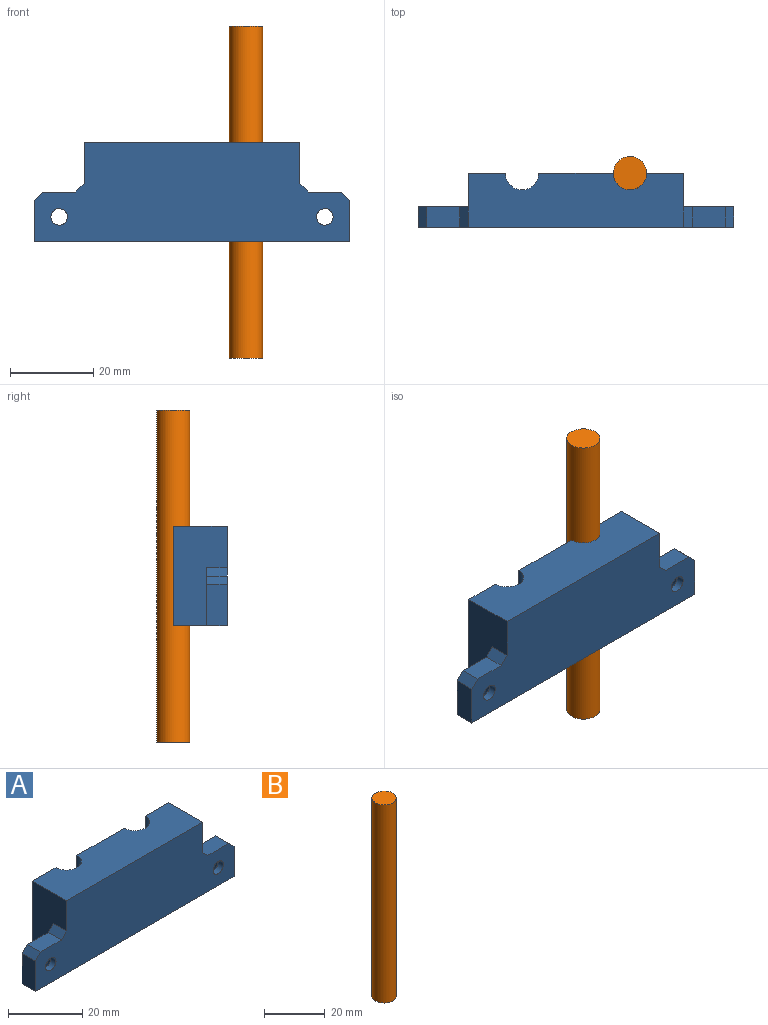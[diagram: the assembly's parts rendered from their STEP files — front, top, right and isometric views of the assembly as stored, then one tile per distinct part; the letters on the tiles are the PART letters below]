
ASSEMBLY  parts=2 mates=1
PART A: 32 faces, bbox 76x13x24 mm
  f0: plane 24x13mm, normal (-1,0,0), area 242mm2, adj f4,f5,f6,f9,f21,f27
  f1: plane 24x12mm, normal (0,0,-1), area 169.6mm2, adj f2,f4,f7,f8
  f2: plane 24x18mm, normal (0,1,0), area 192mm2, adj f1,f3,f6,f7,f8,f9,f10,f11
  f3: cylinder r=4mm len=24mm, axis (0,0,-1), area 301.6mm2, adj f2,f4,f6,f9
  f4: plane 24x9mm, normal (0,1,0), area 96mm2, adj f0,f1,f3,f6,f7,f8,f9,f10
  f5: plane 76x24mm, normal (0,-1,0), area 1510.9mm2, adj f0,f6,f9,f14,f18,f19,f20,f22
  f6: plane 52x13mm, normal (0,0,1), area 625.7mm2, adj f0,f2,f3,f4,f5,f12,f13,f14
  f7: cylinder r=12mm len=24mm, axis (0,0,-1), area 754mm2, adj f1,f2,f4,f10
  f8: cylinder r=6mm len=20mm, axis (0,0,-1), area 377mm2, adj f1,f2,f4,f10
  f9: plane 76x13mm, normal (0,0,-1), area 745.7mm2, adj f0,f2,f3,f4,f5,f12,f13,f14
  f10: plane 24x12mm, normal (0,0,1), area 169.6mm2, adj f2,f4,f7,f8
  f11: plane 24x12mm, normal (0,0,-1), area 169.6mm2, adj f2,f12,f15,f16
  f12: plane 24x9mm, normal (0,1,0), area 96mm2, adj f6,f9,f11,f13,f14,f15,f16,f17
  f13: cylinder r=4mm len=24mm, axis (0,0,-1), area 301.6mm2, adj f2,f6,f9,f12
  f14: plane 24x13mm, normal (1,0,0), area 242mm2, adj f5,f6,f9,f12,f25,f28
  f15: cylinder r=12mm len=24mm, axis (0,0,-1), area 754mm2, adj f2,f11,f12,f17
  f16: cylinder r=6mm len=20mm, axis (0,0,-1), area 377mm2, adj f2,f11,f12,f17
  f17: plane 24x12mm, normal (0,0,1), area 169.6mm2, adj f2,f12,f15,f16
  f18: plane 8x5mm, normal (0,0,1), area 40mm2, adj f5,f21,f26,f27
  f19: plane 10x5mm, normal (-1,0,0), area 50mm2, adj f5,f9,f21,f26
  f20: cylinder r=2mm len=4mm, axis (0,-1,0), area 25.1mm2, adj f5,f31
  f21: plane 14x12mm, normal (0,1,0), area 65.5mm2, adj f0,f9,f18,f19,f26,f27,f31
  f22: plane 10x5mm, normal (1,0,0), area 50mm2, adj f5,f9,f25,f29
  f23: plane 8x5mm, normal (0,0,1), area 40mm2, adj f5,f25,f28,f29
  f24: cylinder r=2mm len=4mm, axis (0,-1,0), area 25.1mm2, adj f5,f30
  f25: plane 14x12mm, normal (0,1,0), area 65.5mm2, adj f9,f14,f22,f23,f28,f29,f30
  f26: plane 5x2mm, normal (-0.71,0,0.71), area 14.1mm2, adj f5,f18,f19,f21
  f27: plane 5x2mm, normal (-0.71,0,0.71), area 14.1mm2, adj f0,f5,f18,f21
  f28: plane 5x2mm, normal (0.71,0,0.71), area 14.1mm2, adj f5,f14,f23,f25
  f29: plane 5x2mm, normal (0.71,0,0.71), area 14.1mm2, adj f5,f22,f23,f25
  f30: cone r=2mm half-angle=45deg, axis (0,1,0), area 93.3mm2, adj f24,f25
  f31: cone r=5mm half-angle=45deg, axis (0,1,0), area 93.3mm2, adj f20,f21
PART B: 3 faces, bbox 8x8x80 mm
  f0: cylinder r=4mm len=80mm, axis (0,0,-1), area 2010.6mm2, adj f1,f2
  f1: plane 8x8mm, normal (0,0,1), area 50.3mm2, adj f0
  f2: plane 8x8mm, normal (0,0,-1), area 50.3mm2, adj f0
PLACE A t=(4.36,-7.45,0)mm fixed
PLACE B t=(30.36,5.55,-40)mm
MATE ball A.f13 <-> B.f0  axis (0,0,-1) through (30.36,5.55,0)mm
